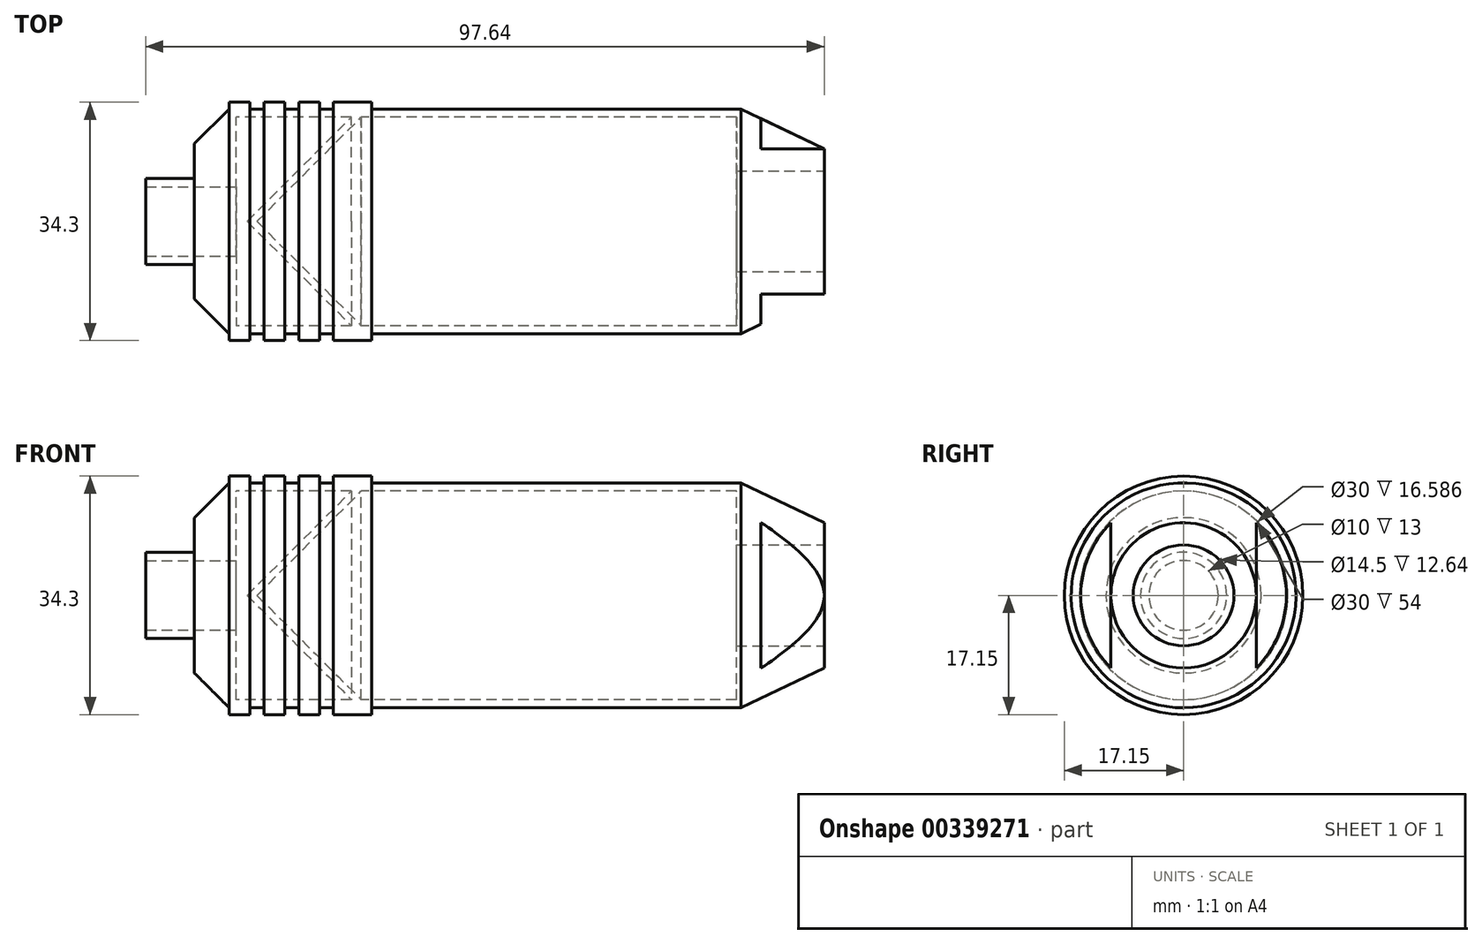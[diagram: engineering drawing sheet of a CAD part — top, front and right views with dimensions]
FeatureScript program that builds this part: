
annotation { "Feature Type Name" : "Feature", "Feature Type Description" : "" }
export const myFeature = defineFeature(function(context is Context, id is Id, definition is map)
    precondition{}
    {
        {
            var Q0;
            Q0=qCreatedBy(makeId("Right.planeOp"),FACE);
            var sketch = newSketch(context, id + "F0", { "sketchPlane" : qUnion([Q0])});
            skCircle(sketch, "E0", {"center": v(0, 0) * mm, "radius": 16.18 * mm});
            skCircle(sketch, "E1", {"center": v(0, 0) * mm, "radius": 17.15 * mm});
            skCircle(sketch, "E2", {"center": v(0, 0) * mm, "radius": 6.2 * mm});
            skCircle(sketch, "E3", {"center": v(0, 0) * mm, "radius": 5 * mm});
            skCircle(sketch, "E4", {"center": v(0, 0) * mm, "radius": 15 * mm});
            skSolve(sketch);
        }
        {
            var Q0;
            Q0=makeQuery(id+"F0.imprint","IMPRINT",FACE,{"disambiguationData":[TD([[makeQuery(id+"F0.imprint","IMPRINT",EDGE,{"derivedFrom":sQuery(id+"F0.wireOp",EDGE,"E0")}),1.0]])]});
            var Q1;
            Q1=makeQuery(id+"F0.imprint","IMPRINT",FACE,{"disambiguationData":[TD([[makeQuery(id+"F0.imprint","IMPRINT",EDGE,{"derivedFrom":sQuery(id+"F0.wireOp",EDGE,"E2")}),-1.0]])]});
            var Q2;
            Q2=makeQuery(id+"F0.imprint","IMPRINT",FACE,{"disambiguationData":[TD([[makeQuery(id+"F0.imprint","IMPRINT",EDGE,{"derivedFrom":sQuery(id+"F0.wireOp",EDGE,"E3")}),1.0]])]});
            var Q3;
            Q3=makeQuery(id+"F0.imprint","IMPRINT",FACE,{"disambiguationData":[TD([[makeQuery(id+"F0.imprint","IMPRINT",EDGE,{"derivedFrom":sQuery(id+"F0.wireOp",EDGE,"E2")}),1.0]])]});
            extrude(context, id + "F1", {"entities" : qUnion([Q0, Q1, Q2, Q3]), "depth" : 90.64 * mm});
        }
        {
            var Q0;
            Q0=makeQuery(id+"F0.imprint","IMPRINT",FACE,{"disambiguationData":[TD([[makeQuery(id+"F0.imprint","IMPRINT",EDGE,{"derivedFrom":sQuery(id+"F0.wireOp",EDGE,"E0")}),-1.0]])]});
            extrude(context, id + "F2", {"entities" : qUnion([Q0]), "operationType" : NewBodyOperationType.ADD, "depth" : 8 * mm, "hasSecondDirection" : true, "secondDirectionOppositeDirection" : false, "secondDirectionDepth" : 5 * mm});
        }
        {
            var Q0;
            Q0=makeQuery(id+"F0.imprint","IMPRINT",FACE,{"disambiguationData":[TD([[makeQuery(id+"F0.imprint","IMPRINT",EDGE,{"derivedFrom":sQuery(id+"F0.wireOp",EDGE,"E0")}),-1.0]])]});
            extrude(context, id + "F3", {"entities" : qUnion([Q0]), "operationType" : NewBodyOperationType.ADD, "depth" : 13 * mm, "hasSecondDirection" : true, "secondDirectionOppositeDirection" : false, "secondDirectionDepth" : 10 * mm});
        }
        {
            var Q0;
            Q0=makeQuery(id+"F0.imprint","IMPRINT",FACE,{"disambiguationData":[TD([[makeQuery(id+"F0.imprint","IMPRINT",EDGE,{"derivedFrom":sQuery(id+"F0.wireOp",EDGE,"E0")}),-1.0]])]});
            extrude(context, id + "F4", {"entities" : qUnion([Q0]), "operationType" : NewBodyOperationType.ADD, "depth" : 18 * mm, "hasSecondDirection" : true, "secondDirectionOppositeDirection" : false, "secondDirectionDepth" : 15 * mm});
        }
        {
            var Q0;
            Q0=makeQuery(id+"F0.imprint","IMPRINT",FACE,{"disambiguationData":[TD([[makeQuery(id+"F0.imprint","IMPRINT",EDGE,{"derivedFrom":sQuery(id+"F0.wireOp",EDGE,"E0")}),-1.0]])]});
            extrude(context, id + "F5", {"entities" : qUnion([Q0]), "operationType" : NewBodyOperationType.ADD, "depth" : 25.5 * mm, "hasSecondDirection" : true, "secondDirectionOppositeDirection" : false, "secondDirectionDepth" : 20 * mm});
        }
        {
            var Q0;
            Q0=makeQuery(id+"F1.opExtrude","CAP_EDGE",EDGE,{"disambiguationData":[OSD([sQuery(id+"F0.wireOp",EDGE,"E0")])],"isStart":true});
            chamfer(context, id + "F6", {"entities" : qUnion([Q0]), "width" : 5 * mm, "tangentPropagation" : true});
        }
        {
            var Q0;
            Q0=makeQuery(id+"F0.imprint","IMPRINT",FACE,{"disambiguationData":[TD([[makeQuery(id+"F0.imprint","IMPRINT",EDGE,{"derivedFrom":sQuery(id+"F0.wireOp",EDGE,"E2")}),1.0]])]});
            extrude(context, id + "F7", {"entities" : qUnion([Q0]), "operationType" : NewBodyOperationType.ADD, "oppositeDirection" : true, "depth" : 7 * mm, "hasSecondDirection" : true, "secondDirectionOppositeDirection" : false, "secondDirectionDepth" : 5 * mm});
        }
        {
            var Q0;
            Q0=makeQuery(id+"F1.opExtrude","CAP_EDGE",EDGE,{"disambiguationData":[OSD([sQuery(id+"F0.wireOp",EDGE,"E0")])],"isStart":false});
            chamfer(context, id + "F8", {"entities" : qUnion([Q0]), "chamferType" : ChamferType.TWO_OFFSETS, "width1" : 5.72 * mm, "oppositeDirection" : false, "width2" : 12 * mm, "tangentPropagation" : true});
        }
        {
            var Q0;
            Q0=makeQuery(id+"F1.opExtrude","CAP_FACE",FACE,{"disambiguationData":[OSD([sQuery(id+"F0.wireOp",EDGE,"E0")])],"isStart":false});
            var sketch = newSketch(context, id + "F9", { "sketchPlane" : qUnion([Q0])});
            skPoint(sketch, "E5", {"position": v(0, 0) * mm});
            skLineSegment(sketch, "E6", {"start": v(0, 16.18) * mm, "end": v(0, -16.18) * mm, "construction": true});
            skLineSegment(sketch, "E7.bottom", {"start": v(10.45, 16.18) * mm, "end": v(16.18, 16.18) * mm});
            skLineSegment(sketch, "E7.top", {"start": v(10.45, -16.18) * mm, "end": v(16.18, -16.18) * mm});
            skLineSegment(sketch, "E7.left", {"start": v(10.45, 16.17) * mm, "end": v(10.45, -16.17) * mm});
            skLineSegment(sketch, "E7.right", {"start": v(16.18, 16.17) * mm, "end": v(16.18, -16.17) * mm});
            skLineSegment(sketch, "E8.MirrorCS", {"start": v(-10.45, -16.18) * mm, "end": v(-16.17, -16.18) * mm});
            skLineSegment(sketch, "E9.MirrorCS", {"start": v(-16.18, 16.17) * mm, "end": v(-16.17, -16.18) * mm});
            skLineSegment(sketch, "E10.MirrorCS", {"start": v(-10.45, 16.17) * mm, "end": v(-10.45, -16.18) * mm});
            skLineSegment(sketch, "E11.MirrorCS", {"start": v(-10.45, 16.18) * mm, "end": v(-16.18, 16.18) * mm});
            skSolve(sketch);
        }
        {
            var Q0;
            {var subQ1=sQuery(id+"F9.wireOp",EDGE,"E8.MirrorCS");Q0=makeQuery(id+"F9.imprint","IMPRINT",FACE,{"disambiguationData":[TD([[makeQuery(id+"F9.imprint","IMPRINT",EDGE,{"derivedFrom":subQ1}),-1.0]])]});}
            var Q1;
            {var subQ4=sQuery(id+"F9.wireOp",EDGE,"E7.bottom");Q1=makeQuery(id+"F9.imprint","IMPRINT",FACE,{"disambiguationData":[TD([[makeQuery(id+"F9.imprint","IMPRINT",EDGE,{"derivedFrom":subQ4}),-1.0]])]});}
            extrude(context, id + "F10", {"entities" : qUnion([Q0, Q1]), "operationType" : NewBodyOperationType.REMOVE, "oppositeDirection" : true, "depth" : 9.1 * mm});
        }
        {
            var Q0;
            Q0=sQuery(id+"F9.wireOp",VERTEX,"E5");
            var Q1;
            Q1=makeQuery(id+"F1.opExtrude","SWEPT_BODY",BODY,{"disambiguationData":[OSD([sQuery(id+"F0.wireOp",EDGE,"E0")])]});
            hole(context, id + "F11", {"style" : HoleStyle.SIMPLE, "endStyle" : HoleEndStyle.BLIND, "standardTappedOrClearance" : lookupTablePath({ "standard" : "ISO", "engagement" : "75%", "pitch" : "1.5 mm", "size" : "M16", "type" : "Tapped" }), "standardBlindInLast" : lookupTablePath({ "standard" : "ISO", "engagement" : "75%", "pitch" : "1.5 mm", "size" : "M16", "type" : "Tapped" }), "holeDiameter" : 14.5 * mm, "showTappedDepth" : true, "holeDepth" : 15 * mm, "tappedDepth" : 10.5 * mm, "tapClearance" : 3, "locations" : qUnion([Q0]), "scope" : qUnion([Q1]), "majorDiameter" : 16 * mm});
        }
        {
            var Q0;
            Q0=makeQuery(id+"F0.imprint","IMPRINT",FACE,{"disambiguationData":[TD([[makeQuery(id+"F0.imprint","IMPRINT",EDGE,{"derivedFrom":sQuery(id+"F0.wireOp",EDGE,"E2")}),-1.0]])]});
            var Q1;
            Q1=makeQuery(id+"F0.imprint","IMPRINT",FACE,{"disambiguationData":[TD([[makeQuery(id+"F0.imprint","IMPRINT",EDGE,{"derivedFrom":sQuery(id+"F0.wireOp",EDGE,"E2")}),1.0]])]});
            var Q2;
            Q2=makeQuery(id+"F0.imprint","IMPRINT",FACE,{"disambiguationData":[TD([[makeQuery(id+"F0.imprint","IMPRINT",EDGE,{"derivedFrom":sQuery(id+"F0.wireOp",EDGE,"E3")}),1.0]])]});
            extrude(context, id + "F12", {"entities" : qUnion([Q0, Q1, Q2]), "operationType" : NewBodyOperationType.REMOVE, "depth" : 78 * mm, "hasSecondDirection" : true, "secondDirectionOppositeDirection" : false, "secondDirectionDepth" : 6 * mm});
        }
        {
            var Q0;
            Q0=makeQuery(id+"F7.boolean.opBoolean","SPLIT",FACE,{"disambiguationData":[TD([makeQuery(id+"F7.opExtrude","SWEPT_FACE",FACE,{"disambiguationData":[OSD([sQuery(id+"F0.wireOp",EDGE,"E3")])]})])],"derivedFrom":makeQuery(id+"F1.opExtrude","CAP_FACE",FACE,{"disambiguationData":[OSD([sQuery(id+"F0.wireOp",EDGE,"E0")])],"isStart":true})});
            extrude(context, id + "F13", {"entities" : qUnion([Q0]), "operationType" : NewBodyOperationType.REMOVE, "oppositeDirection" : true, "depth" : 6 * mm});
        }
        {
            var Q0;
            Q0=qCreatedBy(makeId("Front.planeOp"),FACE);
            var sketch = newSketch(context, id + "F14", { "sketchPlane" : qUnion([Q0])});
            skLineSegment(sketch, "E12.0", {"start": v(6, 15) * mm, "end": v(6, -15) * mm, "construction": true});
            skLineSegment(sketch, "E13.0", {"start": v(78, 15) * mm, "end": v(78, -15) * mm, "construction": true});
            skLineSegment(sketch, "E14", {"start": v(24, 15) * mm, "end": v(9, 0) * mm});
            skLineSegment(sketch, "E15.0", {"start": v(22.59, 15) * mm, "end": v(7.59, 0) * mm});
            skLineSegment(sketch, "E16", {"start": v(22.59, 15) * mm, "end": v(24, 15) * mm});
            skLineSegment(sketch, "E17", {"start": v(7.59, 0) * mm, "end": v(9, 0) * mm});
            skLineSegment(sketch, "E18", {"start": v(6, 15) * mm, "end": v(78, 15) * mm, "construction": true});
            skLineSegment(sketch, "E19", {"start": v(78, -15) * mm, "end": v(6, -15) * mm, "construction": true});
            skLineSegment(sketch, "E20", {"start": v(0, 0) * mm, "end": v(78, 0) * mm, "construction": true});
            skSolve(sketch);
        }
        {
            var Q0;
            Q0=makeQuery(id+"F14.imprint","IMPRINT",FACE,{"disambiguationData":[TD([[makeQuery(id+"F14.imprint","IMPRINT",EDGE,{"derivedFrom":sQuery(id+"F14.wireOp",EDGE,"E14")}),-1.0]])]});
            var Q1;
            Q1=sQuery(id+"F14.wireOp",EDGE,"E20");
            revolve(context, id + "F15", {"operationType" : NewBodyOperationType.ADD, "entities" : qUnion([Q0]), "axis" : qUnion([Q1]), "revolveType" : RevolveType.FULL});
        }
    });
